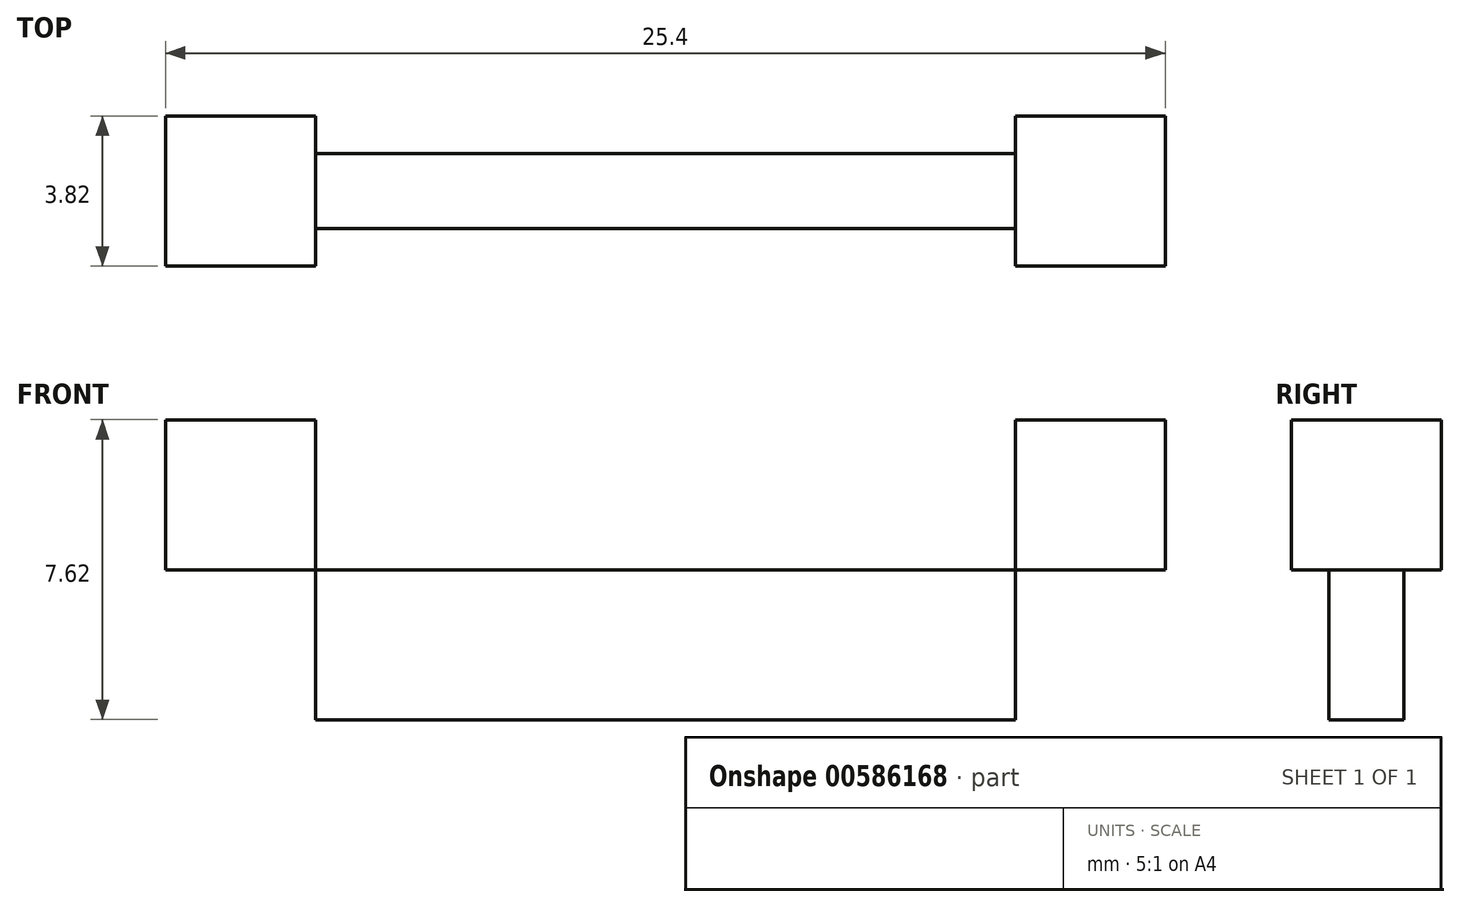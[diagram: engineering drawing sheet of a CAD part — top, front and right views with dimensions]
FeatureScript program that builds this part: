
annotation { "Feature Type Name" : "Feature", "Feature Type Description" : "" }
export const myFeature = defineFeature(function(context is Context, id is Id, definition is map)
    precondition{}
    {
        {
            var Q0;
            Q0=qCreatedBy(makeId("Front.planeOp"),FACE);
            var sketch = newSketch(context, id + "F0", { "sketchPlane" : qUnion([Q0])});
            skLineSegment(sketch, "E0.bottom", {"start": v(12.7, 1.9) * mm, "end": v(-12.7, 1.9) * mm});
            skLineSegment(sketch, "E0.top", {"start": v(12.7, -1.9) * mm, "end": v(-12.7, -1.9) * mm});
            skLineSegment(sketch, "E0.left", {"start": v(12.7, 1.9) * mm, "end": v(12.7, -1.9) * mm});
            skLineSegment(sketch, "E0.right", {"start": v(-12.7, 1.9) * mm, "end": v(-12.7, -1.9) * mm});
            skPoint(sketch, "E0.middle", {"position": v(0, 0) * mm});
            skLineSegment(sketch, "E1.bottom", {"start": v(8.9, -5.72) * mm, "end": v(-8.89, -5.72) * mm});
            skLineSegment(sketch, "E1.top", {"start": v(8.9, 1.9) * mm, "end": v(-8.89, 1.9) * mm});
            skLineSegment(sketch, "E1.left", {"start": v(8.9, -5.72) * mm, "end": v(8.9, 1.9) * mm});
            skLineSegment(sketch, "E1.right", {"start": v(-8.89, -5.72) * mm, "end": v(-8.89, 1.9) * mm});
            skPoint(sketch, "E1.middle", {"position": v(0, -1.9) * mm});
            skSolve(sketch);
        }
        {
            var Q0;
            {var subQ5=sQuery(id+"F0.wireOp",EDGE,"E1.top");Q0=makeQuery(id+"F0.imprint","IMPRINT",FACE,{"disambiguationData":[TD([[makeQuery(id+"F0.imprint","IMPRINT",EDGE,{"derivedFrom":subQ5}),1.0]])]});}
            var Q1;
            {var subQ0=sQuery(id+"F0.wireOp",EDGE,"E0.left");Q1=makeQuery(id+"F0.imprint","IMPRINT",FACE,{"disambiguationData":[TD([[makeQuery(id+"F0.imprint","IMPRINT",EDGE,{"derivedFrom":subQ0}),-1.0]])]});}
            var Q2;
            {var subQ0=sQuery(id+"F0.wireOp",EDGE,"E0.right");Q2=makeQuery(id+"F0.imprint","IMPRINT",FACE,{"disambiguationData":[TD([[makeQuery(id+"F0.imprint","IMPRINT",EDGE,{"derivedFrom":subQ0}),1.0]])]});}
            extrude(context, id + "F1", {"entities" : qUnion([Q0, Q1, Q2]), "endBound" : BoundingType.SYMMETRIC, "depth" : 3.8 * mm, "offsetDistance" : 25.4 * mm});
        }
        {
            var Q0;
            {var subQ5=sQuery(id+"F0.wireOp",EDGE,"E1.bottom");Q0=makeQuery(id+"F0.imprint","IMPRINT",FACE,{"disambiguationData":[TD([[makeQuery(id+"F0.imprint","IMPRINT",EDGE,{"derivedFrom":subQ5}),-1.0]])]});}
            extrude(context, id + "F2", {"entities" : qUnion([Q0]), "operationType" : NewBodyOperationType.ADD, "endBound" : BoundingType.SYMMETRIC, "depth" : 1.9 * mm, "offsetDistance" : 25.4 * mm});
        }
    });
